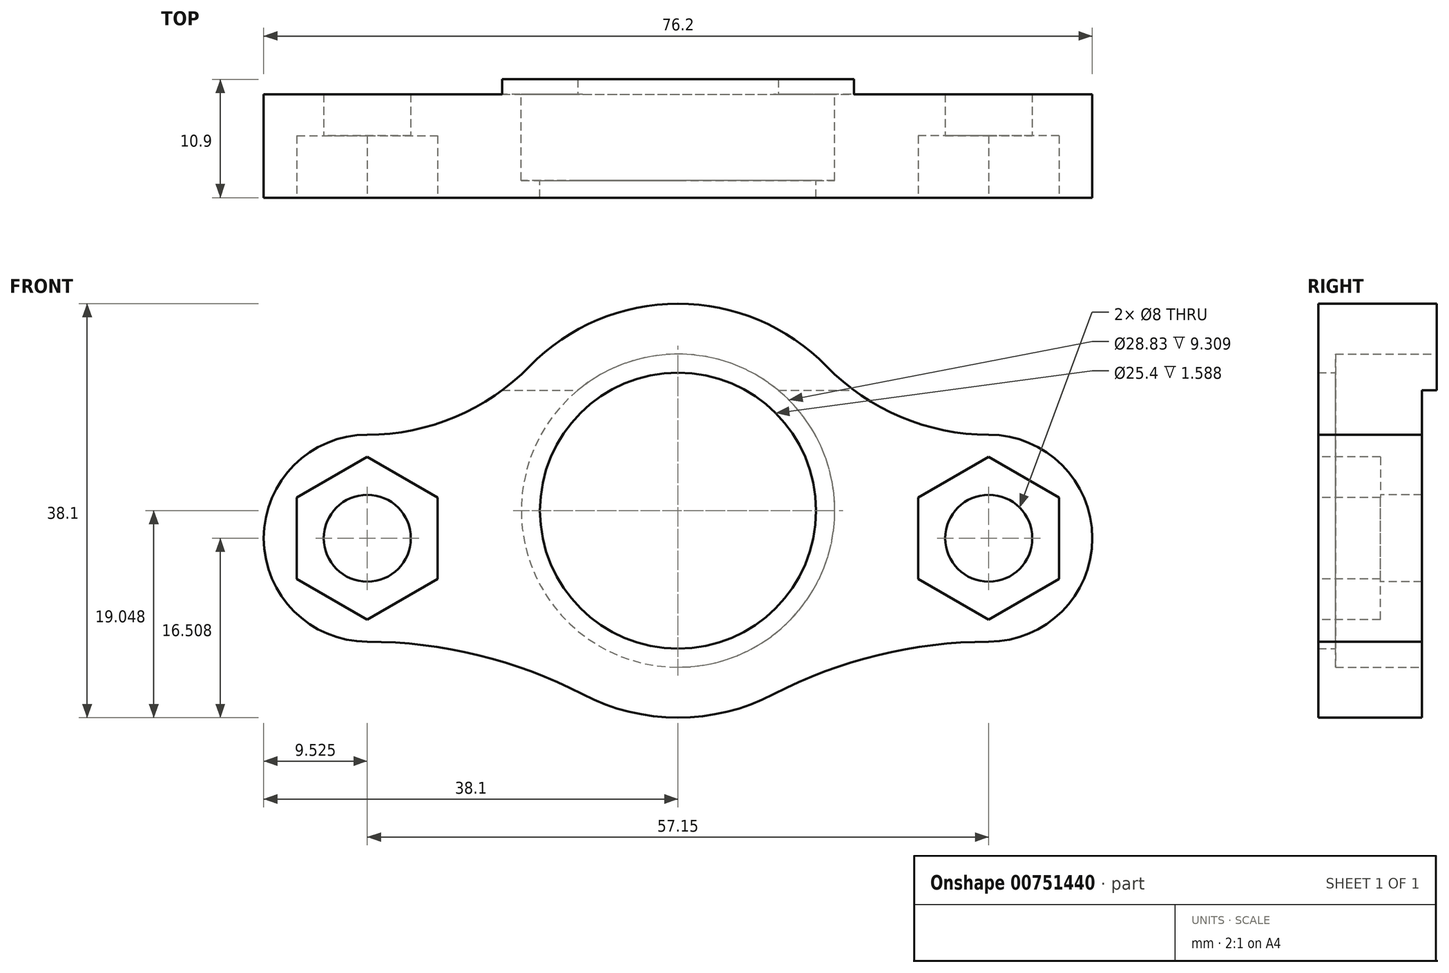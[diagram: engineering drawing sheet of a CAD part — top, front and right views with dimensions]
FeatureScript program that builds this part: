
annotation { "Feature Type Name" : "Feature", "Feature Type Description" : "" }
export const myFeature = defineFeature(function(context is Context, id is Id, definition is map)
    precondition{}
    {
        {
            var Q0;
            Q0=qCreatedBy(makeId("Front.planeOp"),FACE);
            var sketch = newSketch(context, id + "F0", { "sketchPlane" : qUnion([Q0])});
            skLineSegment(sketch, "E0.bottom", {"start": v(-38.1, 15.06) * mm, "end": v(38.1, 15.06) * mm, "construction": true});
            skLineSegment(sketch, "E0.top", {"start": v(-38.1, -15.06) * mm, "end": v(38.1, -15.06) * mm, "construction": true});
            skLineSegment(sketch, "E0.left", {"start": v(-38.1, 15.06) * mm, "end": v(-38.1, -15.06) * mm, "construction": true});
            skLineSegment(sketch, "E0.right", {"start": v(38.1, 15.06) * mm, "end": v(38.1, -15.06) * mm, "construction": true});
            skPoint(sketch, "E1", {"position": v(-38.1, 0) * mm});
            skPoint(sketch, "E2", {"position": v(0, 15.06) * mm});
            skCircle(sketch, "E3", {"center": v(-28.57, 1.45) * mm, "radius": 4.76 * mm, "construction": true});
            skArc(sketch, "E4", {"start": v(-11.11, 6.21) * mm, "mid": v(-15.88, 1.45) * mm, "end": v(-11.11, -3.31) * mm, "construction": true});
            skArc(sketch, "E5", {"start": v(-7.94, -3.31) * mm, "mid": v(-3.17, 1.45) * mm, "end": v(-7.94, 6.21) * mm, "construction": true});
            skLineSegment(sketch, "E6", {"start": v(-11.11, 6.21) * mm, "end": v(-7.94, 6.21) * mm, "construction": true});
            skLineSegment(sketch, "E7", {"start": v(-11.11, -3.31) * mm, "end": v(-7.94, -3.31) * mm, "construction": true});
            skArc(sketch, "E8", {"start": v(7.94, 6.21) * mm, "mid": v(3.18, 1.45) * mm, "end": v(7.94, -3.31) * mm, "construction": true});
            skArc(sketch, "E9", {"start": v(11.11, -3.31) * mm, "mid": v(15.88, 1.45) * mm, "end": v(11.11, 6.21) * mm, "construction": true});
            skLineSegment(sketch, "E10", {"start": v(7.94, 6.21) * mm, "end": v(11.11, 6.21) * mm, "construction": true});
            skLineSegment(sketch, "E11", {"start": v(7.94, -3.31) * mm, "end": v(11.11, -3.31) * mm, "construction": true});
            skCircle(sketch, "E12", {"center": v(28.57, 1.45) * mm, "radius": 4.76 * mm, "construction": true});
            skLineSegment(sketch, "E13.top", {"start": v(-38.1, -13.7) * mm, "end": v(38.1, -13.7) * mm, "construction": true});
            skLineSegment(sketch, "E13.left", {"start": v(-38.1, -15.06) * mm, "end": v(-38.1, -13.7) * mm, "construction": true});
            skLineSegment(sketch, "E13.right", {"start": v(38.1, -15.06) * mm, "end": v(38.1, -13.7) * mm, "construction": true});
            skCircle(sketch, "E14", {"center": v(0, 3.99) * mm, "radius": 6.35 * mm, "construction": true});
            skCircle(sketch, "E15", {"center": v(0, 3.99) * mm, "radius": 14.29 * mm, "construction": true});
            skCircle(sketch, "E16", {"center": v(0, 3.99) * mm, "radius": 50.8 * mm, "construction": true});
            skSolve(sketch);
        }
        {
            var Q0;
            Q0=qCreatedBy(makeId("Front.planeOp"),FACE);
            var sketch = newSketch(context, id + "F1", { "sketchPlane" : qUnion([Q0])});
            skCircle(sketch, "E17", {"center": v(0, 3.99) * mm, "radius": 14.41 * mm});
            skArc(sketch, "E18", {"start": v(-28.57, 10.97) * mm, "mid": v(-38.1, 1.45) * mm, "end": v(-28.58, -8.08) * mm});
            skArc(sketch, "E19", {"start": v(28.57, -8.08) * mm, "mid": v(38.1, 1.45) * mm, "end": v(28.57, 10.97) * mm});
            skArc(sketch, "E20", {"start": v(-8.79, -12.91) * mm, "mid": v(0, -15.06) * mm, "end": v(8.79, -12.91) * mm});
            skLineSegment(sketch, "E21", {"start": v(-28.57, -8.08) * mm, "end": v(-28.57, -8.08) * mm});
            skLineSegment(sketch, "E22", {"start": v(-28.57, 10.97) * mm, "end": v(-28.57, 10.97) * mm});
            skLineSegment(sketch, "E23", {"start": v(28.57, 10.97) * mm, "end": v(28.57, 10.97) * mm});
            skLineSegment(sketch, "E24", {"start": v(28.57, -8.08) * mm, "end": v(28.57, -8.08) * mm});
            skArc(sketch, "E25", {"start": v(-28.57, 10.97) * mm, "mid": v(-20.48, 12.61) * mm, "end": v(-13.65, 17.27) * mm});
            skArc(sketch, "E26", {"start": v(-8.79, -12.91) * mm, "mid": v(-18.4, -9.3) * mm, "end": v(-28.58, -8.08) * mm});
            skArc(sketch, "E27", {"start": v(28.57, -8.08) * mm, "mid": v(18.4, -9.3) * mm, "end": v(8.79, -12.91) * mm});
            skArc(sketch, "E28", {"start": v(13.65, 17.27) * mm, "mid": v(20.48, 12.61) * mm, "end": v(28.57, 10.97) * mm});
            skArc(sketch, "E29.trimOffspring", {"start": v(13.65, 17.27) * mm, "mid": v(0, 23.04) * mm, "end": v(-13.65, 17.27) * mm});
            skLineSegment(sketch, "E30", {"start": v(-16.18, 15.06) * mm, "end": v(16.18, 15.06) * mm});
            skSolve(sketch);
        }
        {
            var Q0;
            Q0=makeQuery(id+"F1.imprint","IMPRINT",FACE,{"disambiguationData":[TD([[makeQuery(id+"F1.imprint","IMPRINT",EDGE,{"derivedFrom":sQuery(id+"F1.wireOp",EDGE,"E17")}),-1.0]])]});
            var Q1;
            {var subQ6=sQuery(id+"F1.wireOp",EDGE,"E18");Q1=makeQuery(id+"F1.imprint","IMPRINT",FACE,{"disambiguationData":[TD([[makeQuery(id+"F1.imprint","IMPRINT",EDGE,{"derivedFrom":subQ6}),1.0]])]});}
            extrude(context, id + "F2", {"entities" : qUnion([Q0, Q1]), "depth" : 7.94 * mm, "offsetDistance" : 25.4 * mm});
        }
        {
            var Q0;
            Q0=makeQuery(id+"F2.opExtrude","CAP_FACE",FACE,{"disambiguationData":[OSD([sQuery(id+"F1.wireOp",EDGE,"E17"),sQuery(id+"F1.wireOp",EDGE,"E18"),sQuery(id+"F1.wireOp",EDGE,"E19"),sQuery(id+"F1.wireOp",EDGE,"E20"),sQuery(id+"F1.wireOp",EDGE,"E25"),sQuery(id+"F1.wireOp",EDGE,"E26"),sQuery(id+"F1.wireOp",EDGE,"E27"),sQuery(id+"F1.wireOp",EDGE,"E28"),sQuery(id+"F1.wireOp",EDGE,"E29.trimOffspring")])],"isStart":false});
            var sketch = newSketch(context, id + "F3", { "sketchPlane" : qUnion([Q0])});
            skCircle(sketch, "E31", {"center": v(0, 3.99) * mm, "radius": 14.41 * mm});
            skCircle(sketch, "E32", {"center": v(0, 3.99) * mm, "radius": 12.7 * mm});
            skSolve(sketch);
        }
        {
            var Q0;
            Q0=makeQuery(id+"F3.imprint","IMPRINT",FACE,{"disambiguationData":[TD([[makeQuery(id+"F3.imprint","IMPRINT",EDGE,{"derivedFrom":sQuery(id+"F3.wireOp",EDGE,"E31")}),-1.0]])]});
            var Q1;
            Q1=makeQuery(id+"F3.imprint","IMPRINT",FACE,{"disambiguationData":[TD([[makeQuery(id+"F3.imprint","IMPRINT",EDGE,{"derivedFrom":sQuery(id+"F3.wireOp",EDGE,"E31")}),1.0]])]});
            extrude(context, id + "F4", {"entities" : qUnion([Q0, Q1]), "operationType" : NewBodyOperationType.ADD, "depth" : 1.59 * mm, "offsetDistance" : 25.4 * mm});
        }
        {
            var Q0;
            Q0=makeQuery(id+"F4.opExtrude","CAP_FACE",FACE,{"disambiguationData":[OSD([sQuery(id+"F1.wireOp",EDGE,"E18"),sQuery(id+"F1.wireOp",EDGE,"E19"),sQuery(id+"F1.wireOp",EDGE,"E20"),sQuery(id+"F1.wireOp",EDGE,"E25"),sQuery(id+"F1.wireOp",EDGE,"E26"),sQuery(id+"F1.wireOp",EDGE,"E27"),sQuery(id+"F1.wireOp",EDGE,"E28"),sQuery(id+"F1.wireOp",EDGE,"E29.trimOffspring"),sQuery(id+"F3.wireOp",EDGE,"E32")])],"isStart":false});
            var sketch = newSketch(context, id + "F5", { "sketchPlane" : qUnion([Q0])});
            skCircle(sketch, "E33", {"center": v(-28.57, 1.45) * mm, "radius": 4 * mm});
            skCircle(sketch, "E34.cCircle", {"center": v(-28.57, 1.45) * mm, "radius": 6.48 * mm, "construction": true});
            skLineSegment(sketch, "E34.0", {"start": v(-22.1, 5.19) * mm, "end": v(-22.1, -2.3) * mm});
            skLineSegment(sketch, "E34.1", {"start": v(-22.1, -2.3) * mm, "end": v(-28.57, -6.03) * mm});
            skLineSegment(sketch, "E34.2", {"start": v(-28.57, -6.03) * mm, "end": v(-35.05, -2.3) * mm});
            skLineSegment(sketch, "E34.3", {"start": v(-35.05, -2.3) * mm, "end": v(-35.05, 5.19) * mm});
            skLineSegment(sketch, "E34.4", {"start": v(-35.05, 5.19) * mm, "end": v(-28.58, 8.93) * mm});
            skLineSegment(sketch, "E34.5", {"start": v(-28.57, 8.93) * mm, "end": v(-22.1, 5.19) * mm});
            skPoint(sketch, "E34.0.midPoint", {"position": v(-22.1, 1.45) * mm});
            skCircle(sketch, "E35", {"center": v(28.57, 1.45) * mm, "radius": 4 * mm});
            skCircle(sketch, "E36.cCircle", {"center": v(28.57, 1.45) * mm, "radius": 6.48 * mm, "construction": true});
            skLineSegment(sketch, "E36.0", {"start": v(22.1, -2.3) * mm, "end": v(22.1, 5.19) * mm});
            skLineSegment(sketch, "E36.1", {"start": v(22.1, 5.19) * mm, "end": v(28.57, 8.93) * mm});
            skLineSegment(sketch, "E36.2", {"start": v(28.57, 8.93) * mm, "end": v(35.05, 5.19) * mm});
            skLineSegment(sketch, "E36.3", {"start": v(35.05, 5.19) * mm, "end": v(35.05, -2.3) * mm});
            skLineSegment(sketch, "E36.4", {"start": v(35.05, -2.3) * mm, "end": v(28.57, -6.03) * mm});
            skLineSegment(sketch, "E36.5", {"start": v(28.57, -6.03) * mm, "end": v(22.1, -2.3) * mm});
            skPoint(sketch, "E36.0.midPoint", {"position": v(22.1, 1.45) * mm});
            skSolve(sketch);
        }
        {
            var Q0;
            Q0=makeQuery(id+"F5.imprint","IMPRINT",FACE,{"disambiguationData":[TD([[makeQuery(id+"F5.imprint","IMPRINT",EDGE,{"derivedFrom":sQuery(id+"F5.wireOp",EDGE,"E33")}),-1.0]])]});
            var Q1;
            Q1=makeQuery(id+"F5.imprint","IMPRINT",FACE,{"disambiguationData":[TD([[makeQuery(id+"F5.imprint","IMPRINT",EDGE,{"derivedFrom":sQuery(id+"F5.wireOp",EDGE,"E35")}),-1.0]])]});
            extrude(context, id + "F6", {"entities" : qUnion([Q0, Q1]), "operationType" : NewBodyOperationType.REMOVE, "oppositeDirection" : true, "depth" : 5.7 * mm, "offsetDistance" : 25.4 * mm});
        }
        {
            var Q0;
            Q0=makeQuery(id+"F6.boolean.opBoolean","SPLIT",FACE,{"disambiguationData":[TD([makeQuery(id+"F6.opExtrude","SWEPT_FACE",FACE,{"disambiguationData":[OSD([sQuery(id+"F5.wireOp",EDGE,"E33")])]})])],"derivedFrom":makeQuery(id+"F4.opExtrude","CAP_FACE",FACE,{"disambiguationData":[OSD([sQuery(id+"F1.wireOp",EDGE,"E18"),sQuery(id+"F1.wireOp",EDGE,"E19"),sQuery(id+"F1.wireOp",EDGE,"E20"),sQuery(id+"F1.wireOp",EDGE,"E25"),sQuery(id+"F1.wireOp",EDGE,"E26"),sQuery(id+"F1.wireOp",EDGE,"E27"),sQuery(id+"F1.wireOp",EDGE,"E28"),sQuery(id+"F1.wireOp",EDGE,"E29.trimOffspring"),sQuery(id+"F3.wireOp",EDGE,"E32")])],"isStart":false})});
            var Q1;
            Q1=makeQuery(id+"F6.boolean.opBoolean","SPLIT",FACE,{"disambiguationData":[TD([makeQuery(id+"F6.opExtrude","SWEPT_FACE",FACE,{"disambiguationData":[OSD([sQuery(id+"F5.wireOp",EDGE,"E35")])]})])],"derivedFrom":makeQuery(id+"F4.opExtrude","CAP_FACE",FACE,{"disambiguationData":[OSD([sQuery(id+"F1.wireOp",EDGE,"E18"),sQuery(id+"F1.wireOp",EDGE,"E19"),sQuery(id+"F1.wireOp",EDGE,"E20"),sQuery(id+"F1.wireOp",EDGE,"E25"),sQuery(id+"F1.wireOp",EDGE,"E26"),sQuery(id+"F1.wireOp",EDGE,"E27"),sQuery(id+"F1.wireOp",EDGE,"E28"),sQuery(id+"F1.wireOp",EDGE,"E29.trimOffspring"),sQuery(id+"F3.wireOp",EDGE,"E32")])],"isStart":false})});
            extrude(context, id + "F7", {"entities" : qUnion([Q0, Q1]), "operationType" : NewBodyOperationType.REMOVE, "endBound" : BoundingType.THROUGH_ALL, "oppositeDirection" : true, "depth" : 25.4 * mm, "offsetDistance" : 25.4 * mm});
        }
        {
            var Q0;
            {var subQ0=sQuery(id+"F1.wireOp",EDGE,"E29.trimOffspring");Q0=makeQuery(id+"F1.imprint","IMPRINT",FACE,{"disambiguationData":[TD([[makeQuery(id+"F1.imprint","IMPRINT",EDGE,{"derivedFrom":subQ0}),1.0]])]});}
            extrude(context, id + "F8", {"entities" : qUnion([Q0]), "operationType" : NewBodyOperationType.ADD, "oppositeDirection" : true, "depth" : 1.37 * mm, "offsetDistance" : 25.4 * mm});
        }
    });
